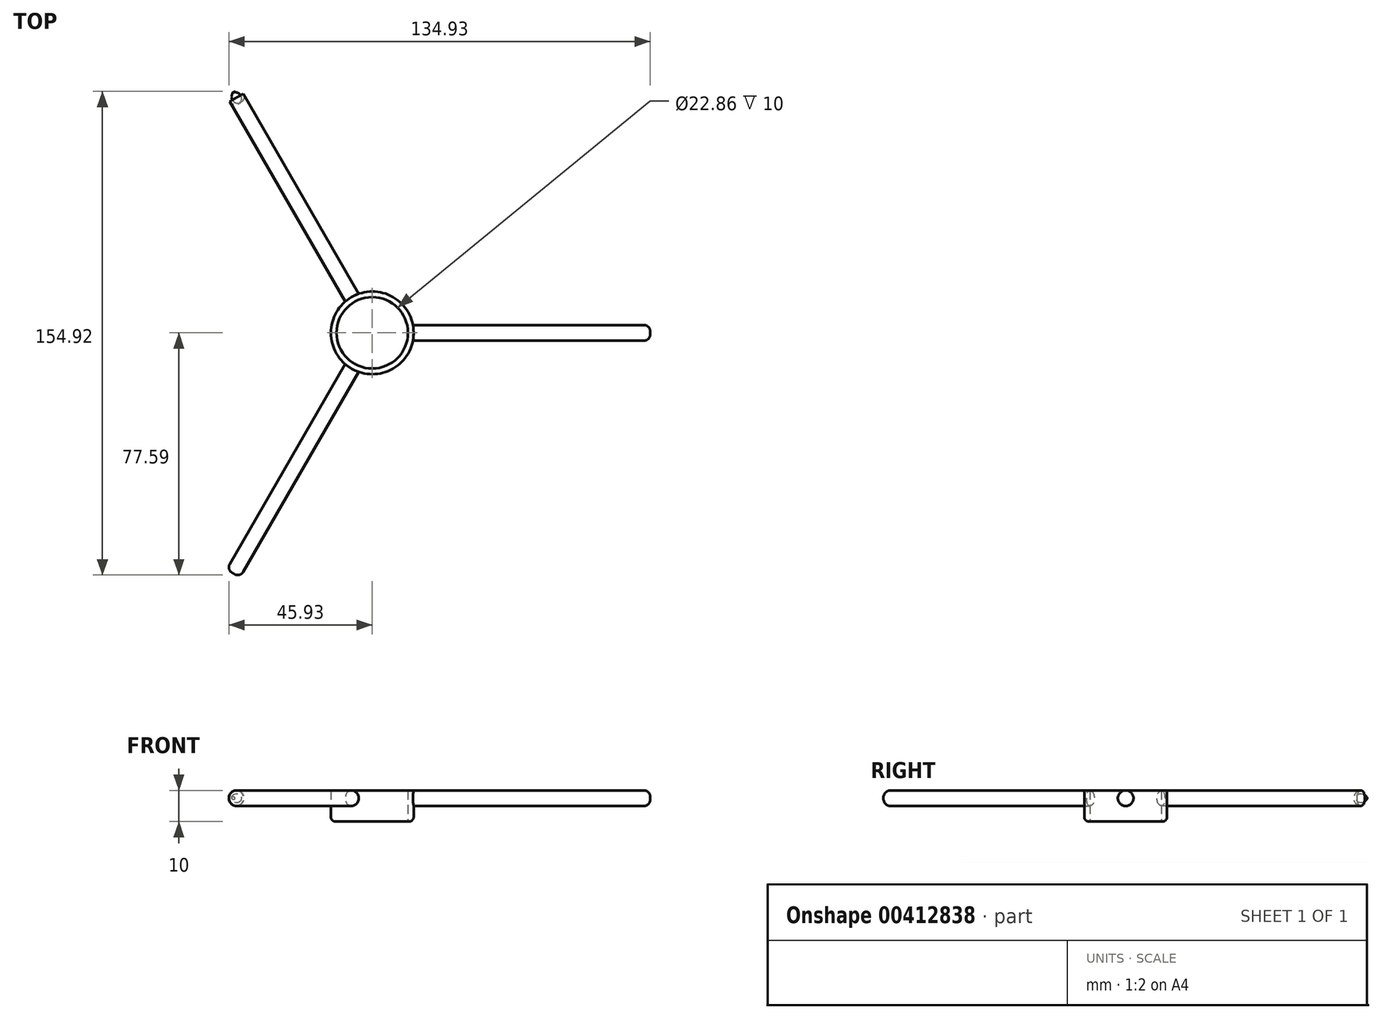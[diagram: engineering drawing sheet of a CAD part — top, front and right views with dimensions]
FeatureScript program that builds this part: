
annotation { "Feature Type Name" : "Feature", "Feature Type Description" : "" }
export const myFeature = defineFeature(function(context is Context, id is Id, definition is map)
    precondition{}
    {
        {
            var Q0;
            Q0=qCreatedBy(makeId("Top.planeOp"),FACE);
            var sketch = newSketch(context, id + "F0", { "sketchPlane" : qUnion([Q0])});
            skCircle(sketch, "E0", {"center": v(0, 0) * mm, "radius": 11.43 * mm});
            skCircle(sketch, "E1", {"center": v(0, 0) * mm, "radius": 13.25 * mm});
            skLineSegment(sketch, "E2", {"start": v(0, 11.43) * mm, "end": v(0, -11.43) * mm});
            skSolve(sketch);
        }
        {
            var Q0;
            Q0 = qSketchRegion(id + "F0", true);
            extrude(context, id + "F1", {"entities" : qUnion([Q0]), "depth" : 10 * mm, "offsetDistance" : 25 * mm});
        }
        {
            var Q0;
            Q0=qCreatedBy(makeId("Right.planeOp"),FACE);
            cPlane(context, id + "F2", {"entities" : qUnion([Q0]), "cplaneType" : CPlaneType.OFFSET, "offset" : 14 * mm, "width" : 150 * mm, "height" : 150 * mm});
        }
        {
            var Q0;
            Q0=qCreatedBy(id+"F2.planeOp",FACE);
            var sketch = newSketch(context, id + "F3", { "sketchPlane" : qUnion([Q0])});
            skCircle(sketch, "E3", {"center": v(0, 7.5) * mm, "radius": 2.5 * mm});
            skSolve(sketch);
        }
        {
            var Q0;
            Q0 = qSketchRegion(id + "F3", true);
            extrude(context, id + "F4", {"entities" : qUnion([Q0]), "operationType" : NewBodyOperationType.ADD, "depth" : 75 * mm, "hasSecondDirection" : true, "secondDirectionOppositeDirection" : true, "secondDirectionDepth" : 2 * mm, "offsetDistance" : 25 * mm});
        }
        {
            var Q0;
            Q0=makeQuery(id+"F1.opExtrude","SWEPT_BODY",BODY,{"disambiguationData":[OSD([sQuery(id+"F0.wireOp",EDGE,"E0"),sQuery(id+"F0.wireOp",EDGE,"E1")])]});
            var Q1;
            Q1=makeQuery(id+"F1.opExtrude","CAP_EDGE",EDGE,{"disambiguationData":[OSD([sQuery(id+"F0.wireOp",EDGE,"E0")])],"isStart":false});
            circularPattern(context, id + "F5", {"operationType" : NewBodyOperationType.ADD, "entities" : qUnion([Q0]), "axis" : qUnion([Q1]), "angle" : 360 * degree, "instanceCount" : 3, "equalSpace" : true});
        }
        {
            var Q0;
            Q0=makeQuery(id+"F1.opExtrude","CAP_EDGE",EDGE,{"disambiguationData":[OSD([sQuery(id+"F0.wireOp",EDGE,"E1")])],"isStart":true});
            fillet(context, id + "F6", {"entities" : qUnion([Q0]), "radius" : 1.5 * mm, "tangentPropagation" : true, "allowEdgeOverflow" : false});
        }
        {
            var Q0;
            Q0=makeQuery(id+"F4.opExtrude","CAP_EDGE",EDGE,{"disambiguationData":[OSD([sQuery(id+"F3.wireOp",EDGE,"E3")])],"isStart":false});
            fillet(context, id + "F7", {"entities" : qUnion([Q0]), "radius" : 2 * mm, "tangentPropagation" : true, "allowEdgeOverflow" : false});
        }
        {
            var Q0;
            Q0=makeQuery(id+"F5.opPattern","COPY",EDGE,{"derivedFrom":makeQuery(id+"F4.opExtrude","CAP_EDGE",EDGE,{"disambiguationData":[OSD([sQuery(id+"F3.wireOp",EDGE,"E3")])],"isStart":false}),"instanceName":"1"});
            fillet(context, id + "F8", {"entities" : qUnion([Q0]), "radius" : 2 * mm, "tangentPropagation" : true, "allowEdgeOverflow" : false});
        }
        {
            var Q0;
            Q0=makeQuery(id+"F5.opPattern","COPY",EDGE,{"derivedFrom":makeQuery(id+"F4.opExtrude","CAP_EDGE",EDGE,{"disambiguationData":[OSD([sQuery(id+"F3.wireOp",EDGE,"E3")])],"isStart":false}),"instanceName":"2"});
            fillet(context, id + "F9", {"entities" : qUnion([Q0]), "radius" : 2 * mm, "tangentPropagation" : true, "allowEdgeOverflow" : false});
        }
    });
